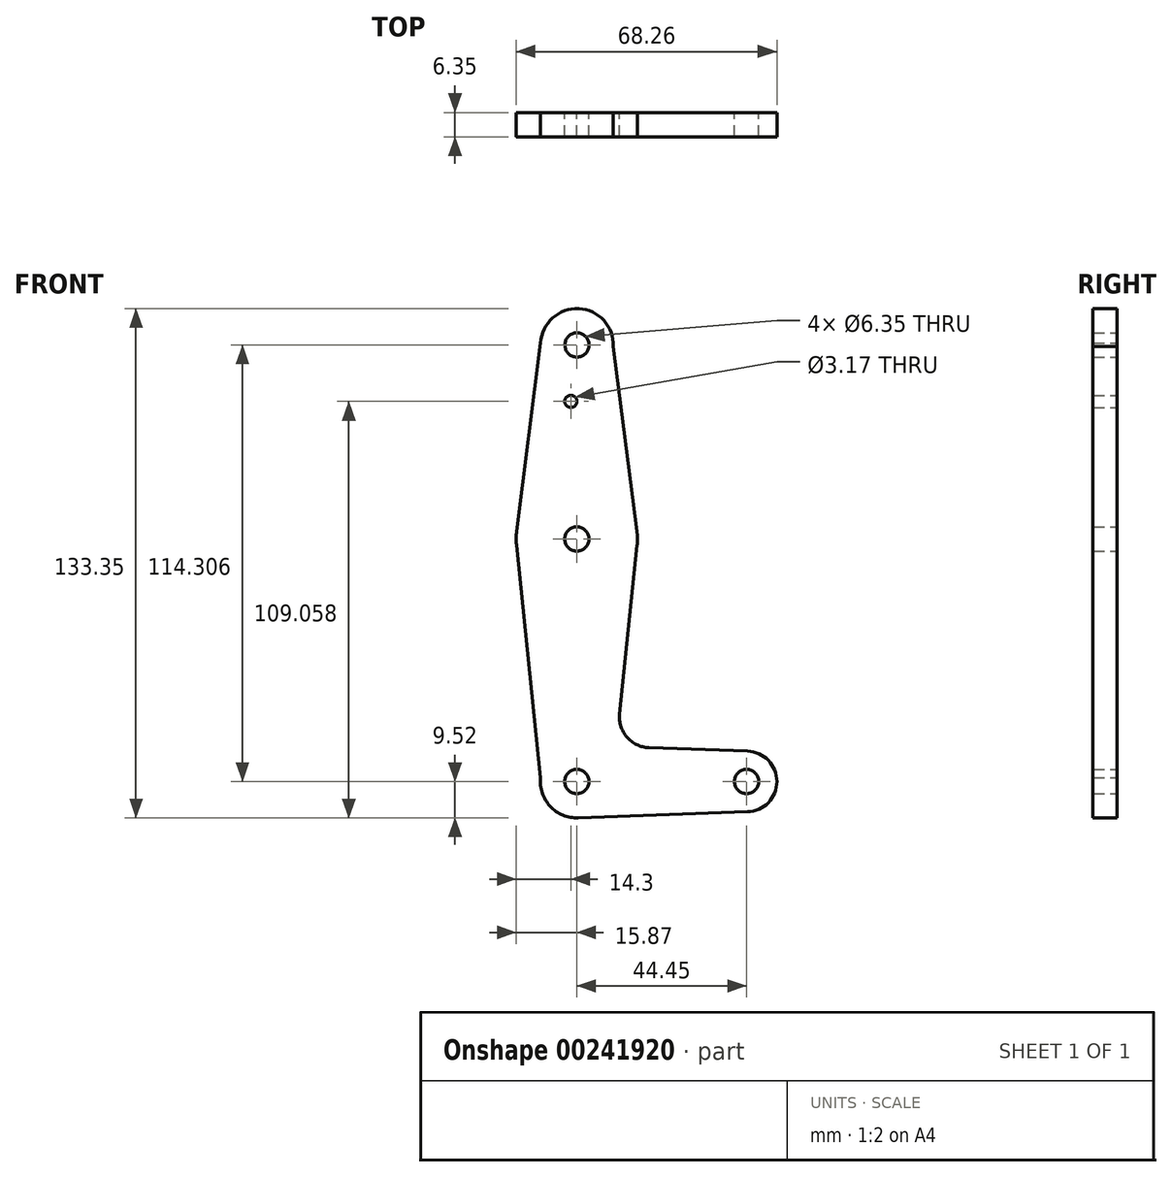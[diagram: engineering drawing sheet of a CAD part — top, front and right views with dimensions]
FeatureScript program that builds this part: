
annotation { "Feature Type Name" : "Feature", "Feature Type Description" : "" }
export const myFeature = defineFeature(function(context is Context, id is Id, definition is map)
    precondition{}
    {
        {
            var Q0;
            Q0=qCreatedBy(makeId("Front.planeOp"),FACE);
            var sketch = newSketch(context, id + "F0", { "sketchPlane" : qUnion([Q0])});
            skCircle(sketch, "E0", {"center": v(0, -63.5) * mm, "radius": 9.53 * mm});
            skCircle(sketch, "E1", {"center": v(0, 0) * mm, "radius": 15.88 * mm});
            skCircle(sketch, "E2", {"center": v(0.04, 50.8) * mm, "radius": 9.53 * mm});
            skCircle(sketch, "E3", {"center": v(44.45, -63.5) * mm, "radius": 3.18 * mm});
            skCircle(sketch, "E4", {"center": v(0.04, 50.8) * mm, "radius": 3.18 * mm});
            skCircle(sketch, "E5", {"center": v(0, 0) * mm, "radius": 3.18 * mm});
            skCircle(sketch, "E6", {"center": v(0, -63.5) * mm, "radius": 3.18 * mm});
            skCircle(sketch, "E7", {"center": v(44.45, -63.5) * mm, "radius": 7.94 * mm});
            skCircle(sketch, "E8", {"center": v(-1.57, 36.04) * mm, "radius": 1.59 * mm});
            skLineSegment(sketch, "E9", {"start": v(-9.47, -62.47) * mm, "end": v(-15.79, -1.64) * mm});
            skLineSegment(sketch, "E10", {"start": v(-9.47, 51.35) * mm, "end": v(-16, 0) * mm});
            skLineSegment(sketch, "E11", {"start": v(9.56, 50.42) * mm, "end": v(15.75, 2.01) * mm});
            skLineSegment(sketch, "E12", {"start": v(11.23, -45.88) * mm, "end": v(15.8, -1.63) * mm});
            skLineSegment(sketch, "E13", {"start": v(44.67, -71.43) * mm, "end": v(0.34, -73.02) * mm});
            skLineSegment(sketch, "E14", {"start": v(44.68, -55.57) * mm, "end": v(18.85, -54.64) * mm});
            skArc(sketch, "E15.filletArc", {"start": v(11.23, -45.88) * mm, "mid": v(13.14, -51.92) * mm, "end": v(18.85, -54.64) * mm});
            skSolve(sketch);
        }
        {
            var Q0;
            Q0 = qSketchRegion(id + "F0", true);
            extrude(context, id + "F1", {"entities" : qUnion([Q0]), "depth" : 6.35 * mm});
        }
    });
